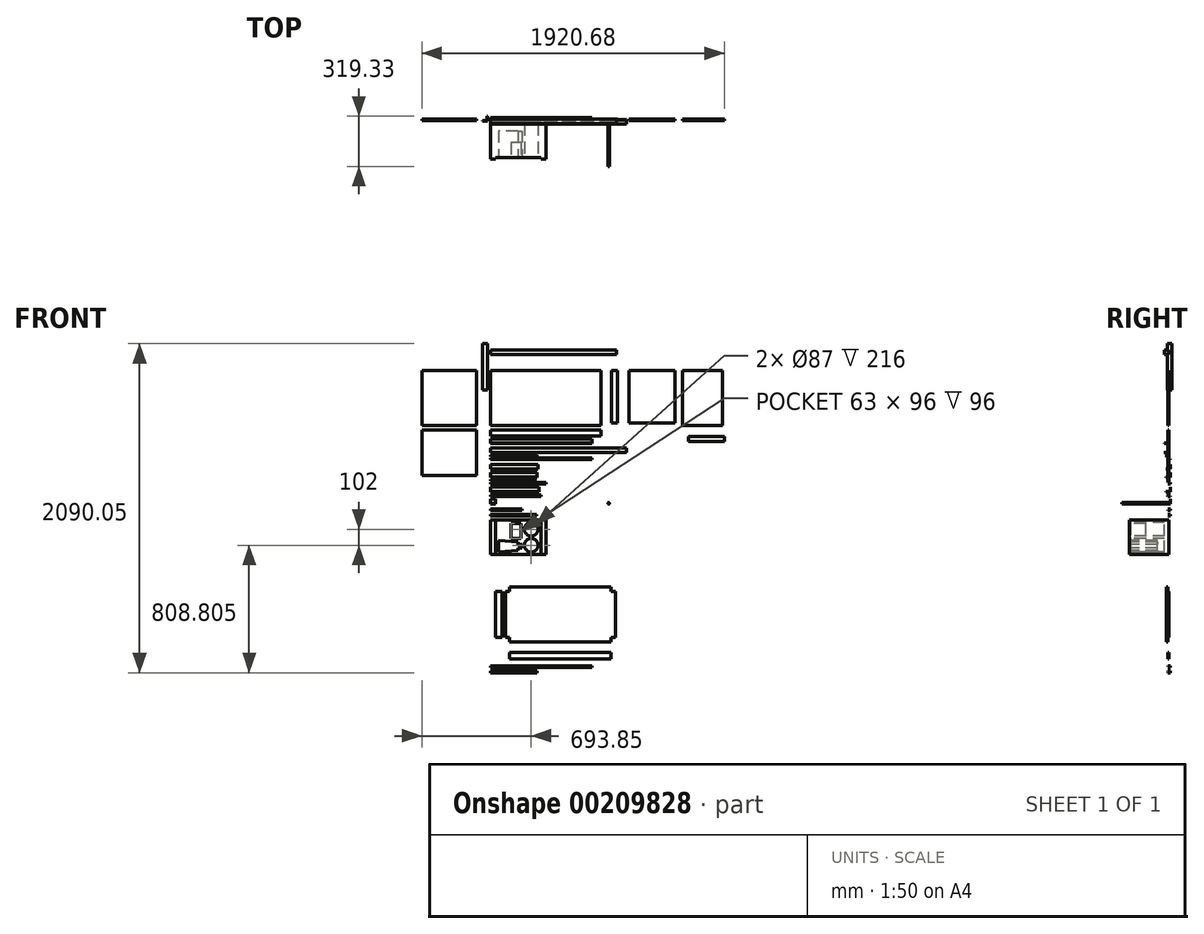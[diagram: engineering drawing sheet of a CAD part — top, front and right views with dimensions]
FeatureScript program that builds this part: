
annotation { "Feature Type Name" : "Feature", "Feature Type Description" : "" }
export const myFeature = defineFeature(function(context is Context, id is Id, definition is map)
    precondition{}
    {
        {
            assignVariable(context, id + "F0", {"name" : "width", "anyValue" : 350});
        }
        {
            assignVariable(context, id + "F1", {"name" : "height", "anyValue" : 800});
        }
        {
            assignVariable(context, id + "F2", {"name" : "length", "anyValue" : 700});
        }
        {
            assignVariable(context, id + "F3", {"name" : "panelW", "anyValue" : 8});
        }
        {
            assignVariable(context, id + "F4", {"name" : "postW", "anyValue" : 28});
        }
        {
            assignVariable(context, id + "F5", {"name" : "sideH", "anyValue" : 40});
        }
        {
            assignVariable(context, id + "F6", {"name" : "profileW", "anyValue" : getVariable(context, 'postW') + 2});
        }
        {
            assignVariable(context, id + "F7", {"name" : "topHeight", "anyValue" : 290});
        }
        {
            assignVariable(context, id + "F8", {"name" : "boxW", "anyValue" : 227});
        }
        {
            assignVariable(context, id + "F9", {"name" : "boxH", "anyValue" : 260});
        }
        {
            assignVariable(context, id + "F10", {"name" : "boxS", "anyValue" : 30});
        }
        {
            var Q0;
            Q0=qCreatedBy(makeId("Front.planeOp"),FACE);
            var sketch = newSketch(context, id + "F11", { "sketchPlane" : qUnion([Q0])});
            skLineSegment(sketch, "E0.bottom", {"start": v(0, 254.27) * mm, "end": v(800, 254.27) * mm});
            skLineSegment(sketch, "E0.top", {"start": v(0, 226.27) * mm, "end": v(800, 226.27) * mm});
            skLineSegment(sketch, "E0.left", {"start": v(0, 254.27) * mm, "end": v(0, 226.27) * mm});
            skLineSegment(sketch, "E0.right", {"start": v(800, 254.27) * mm, "end": v(800, 226.27) * mm});
            skSolve(sketch);
        }
        {
            var Q0;
            Q0=makeQuery(id+"F11.imprint","IMPRINT",FACE,{"disambiguationData":[TD([[makeQuery(id+"F11.imprint","IMPRINT",EDGE,{"derivedFrom":sQuery(id+"F11.wireOp",EDGE,"E0.bottom")}),-1.0]])]});
            extrude(context, id + "F12", {"entities" : qUnion([Q0]), "depth" : (getVariable(context, 'postW')) * mm});
        }
        {
            var Q0;
            Q0=qCreatedBy(makeId("Front.planeOp"),FACE);
            var sketch = newSketch(context, id + "F13", { "sketchPlane" : qUnion([Q0])});
            skLineSegment(sketch, "E1.bottom", {"start": v(0, 124.45) * mm, "end": v(700, 124.45) * mm});
            skLineSegment(sketch, "E1.top", {"start": v(0, -225.55) * mm, "end": v(700, -225.55) * mm});
            skLineSegment(sketch, "E1.left", {"start": v(0, 124.45) * mm, "end": v(0, -225.55) * mm});
            skLineSegment(sketch, "E1.right", {"start": v(700, 124.45) * mm, "end": v(700, -225.55) * mm});
            skSolve(sketch);
        }
        {
            var Q0;
            Q0 = qSketchRegion(id + "F13", true);
            extrude(context, id + "F14", {"entities" : qUnion([Q0]), "depth" : (getVariable(context, 'panelW')) * mm});
        }
        {
            var Q0;
            Q0=qCreatedBy(makeId("Front.planeOp"),FACE);
            var sketch = newSketch(context, id + "F15", { "sketchPlane" : qUnion([Q0])});
            skLineSegment(sketch, "E2.bottom", {"start": v(0, -254.2) * mm, "end": v(700, -254.2) * mm});
            skLineSegment(sketch, "E2.top", {"start": v(0, -294.2) * mm, "end": v(700, -294.2) * mm});
            skLineSegment(sketch, "E2.left", {"start": v(0, -254.2) * mm, "end": v(0, -294.2) * mm});
            skLineSegment(sketch, "E2.right", {"start": v(700, -254.2) * mm, "end": v(700, -294.2) * mm});
            skSolve(sketch);
        }
        {
            var Q0;
            Q0 = qSketchRegion(id + "F15", true);
            extrude(context, id + "F16", {"entities" : qUnion([Q0]), "depth" : (getVariable(context, 'panelW')) * mm});
        }
        {
            var Q0;
            Q0=qCreatedBy(makeId("Front.planeOp"),FACE);
            var sketch = newSketch(context, id + "F17", { "sketchPlane" : qUnion([Q0])});
            skLineSegment(sketch, "E3.bottom", {"start": v(766.47, 124.45) * mm, "end": v(806.47, 124.45) * mm});
            skLineSegment(sketch, "E3.top", {"start": v(766.47, -209.55) * mm, "end": v(806.47, -209.55) * mm});
            skLineSegment(sketch, "E3.left", {"start": v(766.47, 124.45) * mm, "end": v(766.47, -209.55) * mm});
            skLineSegment(sketch, "E3.right", {"start": v(806.47, 124.45) * mm, "end": v(806.47, -209.55) * mm});
            skSolve(sketch);
        }
        {
            var Q0;
            Q0 = qSketchRegion(id + "F17", true);
            extrude(context, id + "F18", {"entities" : qUnion([Q0]), "depth" : (getVariable(context, 'panelW')) * mm});
        }
        {
            var Q0;
            Q0=qCreatedBy(makeId("Right.planeOp"),FACE);
            var sketch = newSketch(context, id + "F19", { "sketchPlane" : qUnion([Q0])});
            skLineSegment(sketch, "E4", {"start": v(0, -310.42) * mm, "end": v(0, -340.42) * mm});
            skLineSegment(sketch, "E5", {"start": v(0, -340.42) * mm, "end": v(-30, -340.42) * mm});
            skLineSegment(sketch, "E6", {"start": v(-30, -340.42) * mm, "end": v(-30, -338.42) * mm});
            skLineSegment(sketch, "E7", {"start": v(-30, -338.42) * mm, "end": v(-2, -338.42) * mm});
            skLineSegment(sketch, "E8", {"start": v(-2, -338.42) * mm, "end": v(-2, -310.42) * mm});
            skLineSegment(sketch, "E9", {"start": v(-2, -310.42) * mm, "end": v(0, -310.42) * mm});
            skSolve(sketch);
        }
        {
            var Q0;
            Q0 = qSketchRegion(id + "F19", true);
            extrude(context, id + "F20", {"entities" : qUnion([Q0]), "depth" : (getVariable(context, 'length') - 2 * getVariable(context, 'postW')) * mm});
        }
        {
            var Q0;
            Q0=qCreatedBy(makeId("Top.planeOp"),FACE);
            var sketch = newSketch(context, id + "F21", { "sketchPlane" : qUnion([Q0])});
            skLineSegment(sketch, "E10", {"start": v(-21.86, 19.33) * mm, "end": v(-21.86, -10.67) * mm});
            skLineSegment(sketch, "E11", {"start": v(-21.86, -10.67) * mm, "end": v(-51.86, -10.67) * mm});
            skLineSegment(sketch, "E12", {"start": v(-51.86, -10.67) * mm, "end": v(-51.86, -8.67) * mm});
            skLineSegment(sketch, "E13", {"start": v(-51.86, -8.67) * mm, "end": v(-23.86, -8.67) * mm});
            skLineSegment(sketch, "E14", {"start": v(-23.86, -8.67) * mm, "end": v(-23.86, 19.33) * mm});
            skLineSegment(sketch, "E15", {"start": v(-23.86, 19.33) * mm, "end": v(-21.86, 19.33) * mm});
            skSolve(sketch);
        }
        {
            var Q0;
            Q0 = qSketchRegion(id + "F21", true);
            extrude(context, id + "F22", {"entities" : qUnion([Q0]), "depth" : (getVariable(context, 'width') - 2 * getVariable(context, 'postW')) * mm});
        }
        {
            var Q0;
            Q0=makeQuery(id+"F14.opExtrude","SWEPT_FACE",FACE,{"disambiguationData":[OSD([sQuery(id+"F13.wireOp",EDGE,"E1.left")])]});
            var Q1;
            Q1=makeQuery(id+"F14.opExtrude","SWEPT_FACE",FACE,{"disambiguationData":[OSD([sQuery(id+"F13.wireOp",EDGE,"E1.right")])]});
            cPlane(context, id + "F23", {"entities" : qUnion([Q0, Q1]), "cplaneType" : CPlaneType.MID_PLANE, "offset" : 25 * mm, "width" : 150 * mm, "height" : 150 * mm});
        }
        {
            var Q0;
            Q0=qCreatedBy(makeId("Right.planeOp"),FACE);
            var sketch = newSketch(context, id + "F24", { "sketchPlane" : qUnion([Q0])});
            skLineSegment(sketch, "E16", {"start": v(-1.9, -368) * mm, "end": v(-1.9, -398) * mm});
            skLineSegment(sketch, "E17", {"start": v(-1.9, -398) * mm, "end": v(-31.9, -398) * mm});
            skLineSegment(sketch, "E18", {"start": v(-31.9, -398) * mm, "end": v(-31.9, -396) * mm});
            skLineSegment(sketch, "E19", {"start": v(-31.9, -396) * mm, "end": v(-3.9, -396) * mm});
            skLineSegment(sketch, "E20", {"start": v(-3.9, -396) * mm, "end": v(-3.9, -368) * mm});
            skLineSegment(sketch, "E21", {"start": v(-3.9, -368) * mm, "end": v(-1.9, -368) * mm});
            skSolve(sketch);
        }
        {
            var Q0;
            Q0 = qSketchRegion(id + "F24", true);
            extrude(context, id + "F25", {"entities" : qUnion([Q0]), "depth" : (getVariable(context, 'height') + getVariable(context, 'sideH') + 2 * getVariable(context, 'panelW') + 6) * mm});
        }
        {
            var Q0;
            Q0=qCreatedBy(makeId("Right.planeOp"),FACE);
            var sketch = newSketch(context, id + "F26", { "sketchPlane" : qUnion([Q0])});
            skLineSegment(sketch, "E22", {"start": v(0, -412.2) * mm, "end": v(-20.5, -412.2) * mm});
            skLineSegment(sketch, "E23", {"start": v(-20.5, -412.2) * mm, "end": v(-17.5, -415.2) * mm});
            skLineSegment(sketch, "E24", {"start": v(-17.5, -415.2) * mm, "end": v(-20.5, -418.2) * mm});
            skLineSegment(sketch, "E25", {"start": v(-20.5, -418.2) * mm, "end": v(-16.5, -422.2) * mm});
            skLineSegment(sketch, "E26", {"start": v(-16.5, -422.2) * mm, "end": v(0, -422.2) * mm});
            skLineSegment(sketch, "E27", {"start": v(0, -422.2) * mm, "end": v(0, -420.7) * mm});
            skLineSegment(sketch, "E28", {"start": v(0, -420.7) * mm, "end": v(-14.5, -420.7) * mm});
            skLineSegment(sketch, "E29", {"start": v(-14.5, -420.7) * mm, "end": v(-14.5, -413.7) * mm});
            skLineSegment(sketch, "E30", {"start": v(-14.5, -413.7) * mm, "end": v(0, -413.7) * mm});
            skLineSegment(sketch, "E31", {"start": v(0, -413.7) * mm, "end": v(0, -412.2) * mm});
            skSolve(sketch);
        }
        {
            var Q0;
            Q0 = qSketchRegion(id + "F26", true);
            extrude(context, id + "F27", {"entities" : qUnion([Q0]), "depth" : (getVariable(context, 'width') - 2 * getVariable(context, 'postW')) * mm});
        }
        {
            var Q0;
            Q0=qCreatedBy(makeId("Right.planeOp"),FACE);
            var sketch = newSketch(context, id + "F28", { "sketchPlane" : qUnion([Q0])});
            skLineSegment(sketch, "E32", {"start": v(10.4, -431.26) * mm, "end": v(-10.1, -431.26) * mm});
            skLineSegment(sketch, "E33", {"start": v(-10.1, -431.26) * mm, "end": v(-7.1, -434.26) * mm});
            skLineSegment(sketch, "E34", {"start": v(-7.1, -434.26) * mm, "end": v(-10.1, -437.26) * mm});
            skLineSegment(sketch, "E35", {"start": v(-10.1, -437.26) * mm, "end": v(-6.1, -441.26) * mm});
            skLineSegment(sketch, "E36", {"start": v(-6.1, -441.26) * mm, "end": v(10.4, -441.26) * mm});
            skLineSegment(sketch, "E37", {"start": v(10.4, -441.26) * mm, "end": v(10.4, -439.76) * mm});
            skLineSegment(sketch, "E38", {"start": v(10.4, -439.76) * mm, "end": v(-4.1, -439.76) * mm});
            skLineSegment(sketch, "E39", {"start": v(-4.1, -439.76) * mm, "end": v(-4.1, -432.76) * mm});
            skLineSegment(sketch, "E40", {"start": v(-4.1, -432.76) * mm, "end": v(10.4, -432.76) * mm});
            skLineSegment(sketch, "E41", {"start": v(10.4, -432.76) * mm, "end": v(10.4, -431.26) * mm});
            skSolve(sketch);
        }
        {
            var Q0;
            Q0 = qSketchRegion(id + "F28", true);
            extrude(context, id + "F29", {"entities" : qUnion([Q0]), "depth" : (getVariable(context, 'length') - 2 * getVariable(context, 'postW')) * mm});
        }
        {
            var Q0;
            Q0=qCreatedBy(makeId("Front.planeOp"),FACE);
            var sketch = newSketch(context, id + "F30", { "sketchPlane" : qUnion([Q0])});
            skLineSegment(sketch, "E42.bottom", {"start": v(879.27, 124.45) * mm, "end": v(1169.27, 124.45) * mm});
            skLineSegment(sketch, "E42.top", {"start": v(879.27, -209.55) * mm, "end": v(1169.27, -209.55) * mm});
            skLineSegment(sketch, "E42.left", {"start": v(879.27, 124.45) * mm, "end": v(879.27, -209.55) * mm});
            skLineSegment(sketch, "E42.right", {"start": v(1169.27, 124.45) * mm, "end": v(1169.27, -209.55) * mm});
            skSolve(sketch);
        }
        {
            var Q0;
            Q0 = qSketchRegion(id + "F30", true);
            extrude(context, id + "F31", {"entities" : qUnion([Q0]), "depth" : (getVariable(context, 'panelW')) * mm});
        }
        {
            var Q0;
            Q0=qCreatedBy(makeId("Front.planeOp"),FACE);
            var sketch = newSketch(context, id + "F32", { "sketchPlane" : qUnion([Q0])});
            skLineSegment(sketch, "E43.bottom", {"start": v(-88.85, 124.45) * mm, "end": v(-437.35, 124.45) * mm});
            skLineSegment(sketch, "E43.top", {"start": v(-88.85, -225.55) * mm, "end": v(-437.35, -225.55) * mm});
            skLineSegment(sketch, "E43.left", {"start": v(-88.85, 124.45) * mm, "end": v(-88.85, -225.55) * mm});
            skLineSegment(sketch, "E43.right", {"start": v(-437.35, 124.45) * mm, "end": v(-437.35, -225.55) * mm});
            skSolve(sketch);
        }
        {
            var Q0;
            Q0 = qSketchRegion(id + "F32", true);
            extrude(context, id + "F33", {"entities" : qUnion([Q0]), "depth" : (getVariable(context, 'panelW')) * mm});
        }
        {
            var Q0;
            Q0=qCreatedBy(makeId("Front.planeOp"),FACE);
            var sketch = newSketch(context, id + "F34", { "sketchPlane" : qUnion([Q0])});
            skLineSegment(sketch, "E44.bottom", {"start": v(-437.35, -254.2) * mm, "end": v(-88.85, -254.2) * mm});
            skLineSegment(sketch, "E44.top", {"start": v(-437.35, -544.2) * mm, "end": v(-88.85, -544.2) * mm});
            skLineSegment(sketch, "E44.left", {"start": v(-437.35, -254.2) * mm, "end": v(-437.35, -544.2) * mm});
            skLineSegment(sketch, "E44.right", {"start": v(-88.85, -254.2) * mm, "end": v(-88.85, -544.2) * mm});
            skSolve(sketch);
        }
        {
            var Q0;
            Q0 = qSketchRegion(id + "F34", true);
            extrude(context, id + "F35", {"entities" : qUnion([Q0]), "depth" : (getVariable(context, 'panelW')) * mm});
        }
        {
            var Q0;
            Q0=qCreatedBy(makeId("Right.planeOp"),FACE);
            var sketch = newSketch(context, id + "F36", { "sketchPlane" : qUnion([Q0])});
            skLineSegment(sketch, "E45", {"start": v(10.67, -472.68) * mm, "end": v(10.67, -502.68) * mm});
            skLineSegment(sketch, "E46", {"start": v(10.67, -502.68) * mm, "end": v(-19.33, -502.68) * mm});
            skLineSegment(sketch, "E47", {"start": v(-19.33, -502.68) * mm, "end": v(-19.33, -500.68) * mm});
            skLineSegment(sketch, "E48", {"start": v(-19.33, -500.68) * mm, "end": v(8.67, -500.68) * mm});
            skLineSegment(sketch, "E49", {"start": v(8.67, -500.68) * mm, "end": v(8.67, -472.68) * mm});
            skLineSegment(sketch, "E50", {"start": v(8.67, -472.68) * mm, "end": v(10.67, -472.68) * mm});
            skSolve(sketch);
        }
        {
            var Q0;
            Q0 = qSketchRegion(id + "F36", true);
            extrude(context, id + "F37", {"entities" : qUnion([Q0]), "depth" : (getVariable(context, 'topHeight') + getVariable(context, 'panelW') + 2) * mm});
        }
        {
            var Q0;
            Q0=qCreatedBy(makeId("Right.planeOp"),FACE);
            var sketch = newSketch(context, id + "F38", { "sketchPlane" : qUnion([Q0])});
            skLineSegment(sketch, "E51", {"start": v(10.67, -524.8) * mm, "end": v(10.67, -554.8) * mm});
            skLineSegment(sketch, "E52", {"start": v(10.67, -554.8) * mm, "end": v(-19.33, -554.8) * mm});
            skLineSegment(sketch, "E53", {"start": v(-19.33, -554.8) * mm, "end": v(-19.33, -552.8) * mm});
            skLineSegment(sketch, "E54", {"start": v(-19.33, -552.8) * mm, "end": v(8.67, -552.8) * mm});
            skLineSegment(sketch, "E55", {"start": v(8.67, -552.8) * mm, "end": v(8.67, -524.8) * mm});
            skLineSegment(sketch, "E56", {"start": v(8.67, -524.8) * mm, "end": v(10.67, -524.8) * mm});
            skSolve(sketch);
        }
        {
            var Q0;
            Q0 = qSketchRegion(id + "F38", true);
            extrude(context, id + "F39", {"entities" : qUnion([Q0]), "depth" : (getVariable(context, 'width') - 2 * getVariable(context, 'profileW') + 2 * 2) * mm});
        }
        {
            var Q0;
            Q0=qCreatedBy(makeId("Right.planeOp"),FACE);
            var sketch = newSketch(context, id + "F40", { "sketchPlane" : qUnion([Q0])});
            skLineSegment(sketch, "E57", {"start": v(-16.5, -568.56) * mm, "end": v(0, -568.56) * mm});
            skLineSegment(sketch, "E58", {"start": v(0, -568.56) * mm, "end": v(0, -578.56) * mm});
            skLineSegment(sketch, "E59", {"start": v(0, -578.56) * mm, "end": v(-16.5, -578.56) * mm});
            skLineSegment(sketch, "E60", {"start": v(-16.5, -578.56) * mm, "end": v(-16.5, -577.06) * mm});
            skLineSegment(sketch, "E61", {"start": v(-16.5, -577.06) * mm, "end": v(-1.5, -577.06) * mm});
            skLineSegment(sketch, "E62", {"start": v(-1.5, -577.06) * mm, "end": v(-1.5, -570.06) * mm});
            skLineSegment(sketch, "E63", {"start": v(-1.5, -570.06) * mm, "end": v(-16.5, -570.06) * mm});
            skLineSegment(sketch, "E64", {"start": v(-16.5, -570.06) * mm, "end": v(-16.5, -568.56) * mm});
            skSolve(sketch);
        }
        {
            var Q0;
            Q0 = qSketchRegion(id + "F40", true);
            extrude(context, id + "F41", {"entities" : qUnion([Q0]), "depth" : (getVariable(context, 'topHeight') - 7.5) * mm});
        }
        {
            var Q0;
            Q0=qCreatedBy(makeId("Right.planeOp"),FACE);
            var sketch = newSketch(context, id + "F42", { "sketchPlane" : qUnion([Q0])});
            skLineSegment(sketch, "E65", {"start": v(-7.75, -587.4) * mm, "end": v(8.75, -587.4) * mm});
            skLineSegment(sketch, "E66", {"start": v(8.75, -587.4) * mm, "end": v(8.75, -597.4) * mm});
            skLineSegment(sketch, "E67", {"start": v(8.75, -597.4) * mm, "end": v(-7.75, -597.4) * mm});
            skLineSegment(sketch, "E68", {"start": v(-7.75, -597.4) * mm, "end": v(-7.75, -595.9) * mm});
            skLineSegment(sketch, "E69", {"start": v(-7.75, -595.9) * mm, "end": v(7.25, -595.9) * mm});
            skLineSegment(sketch, "E70", {"start": v(7.25, -595.9) * mm, "end": v(7.25, -588.9) * mm});
            skLineSegment(sketch, "E71", {"start": v(7.25, -588.9) * mm, "end": v(-7.75, -588.9) * mm});
            skLineSegment(sketch, "E72", {"start": v(-7.75, -588.9) * mm, "end": v(-7.75, -587.4) * mm});
            skSolve(sketch);
        }
        {
            var Q0;
            Q0 = qSketchRegion(id + "F42", true);
            extrude(context, id + "F43", {"entities" : qUnion([Q0]), "depth" : (getVariable(context, 'width')) * mm});
        }
        {
            var Q0;
            Q0=qCreatedBy(makeId("Right.planeOp"),FACE);
            var sketch = newSketch(context, id + "F44", { "sketchPlane" : qUnion([Q0])});
            skLineSegment(sketch, "E73", {"start": v(10.67, -616.68) * mm, "end": v(10.67, -646.68) * mm});
            skLineSegment(sketch, "E74", {"start": v(10.67, -646.68) * mm, "end": v(-19.33, -646.68) * mm});
            skLineSegment(sketch, "E75", {"start": v(-19.33, -646.68) * mm, "end": v(-19.33, -644.68) * mm});
            skLineSegment(sketch, "E76", {"start": v(-19.33, -644.68) * mm, "end": v(8.67, -644.68) * mm});
            skLineSegment(sketch, "E77", {"start": v(8.67, -644.68) * mm, "end": v(8.67, -616.68) * mm});
            skLineSegment(sketch, "E78", {"start": v(8.67, -616.68) * mm, "end": v(10.67, -616.68) * mm});
            skSolve(sketch);
        }
        {
            var Q0;
            Q0 = qSketchRegion(id + "F44", true);
            extrude(context, id + "F45", {"entities" : qUnion([Q0]), "depth" : (getVariable(context, 'length') / 2 - 1.5 - getVariable(context, 'profileW') + 2 - 15) * mm});
        }
        {
            var Q0;
            Q0=qCreatedBy(makeId("Right.planeOp"),FACE);
            var sketch = newSketch(context, id + "F46", { "sketchPlane" : qUnion([Q0])});
            skLineSegment(sketch, "E79", {"start": v(10.4, -665.74) * mm, "end": v(-10.1, -665.74) * mm});
            skLineSegment(sketch, "E80", {"start": v(-10.1, -665.74) * mm, "end": v(-7.1, -668.74) * mm});
            skLineSegment(sketch, "E81", {"start": v(-7.1, -668.74) * mm, "end": v(-10.1, -671.74) * mm});
            skLineSegment(sketch, "E82", {"start": v(-10.1, -671.74) * mm, "end": v(-6.1, -675.74) * mm});
            skLineSegment(sketch, "E83", {"start": v(-6.1, -675.74) * mm, "end": v(10.4, -675.74) * mm});
            skLineSegment(sketch, "E84", {"start": v(10.4, -675.74) * mm, "end": v(10.4, -674.24) * mm});
            skLineSegment(sketch, "E85", {"start": v(10.4, -674.24) * mm, "end": v(-4.1, -674.24) * mm});
            skLineSegment(sketch, "E86", {"start": v(-4.1, -674.24) * mm, "end": v(-4.1, -667.24) * mm});
            skLineSegment(sketch, "E87", {"start": v(-4.1, -667.24) * mm, "end": v(10.4, -667.24) * mm});
            skLineSegment(sketch, "E88", {"start": v(10.4, -667.24) * mm, "end": v(10.4, -665.74) * mm});
            skSolve(sketch);
        }
        {
            var Q0;
            Q0 = qSketchRegion(id + "F46", true);
            extrude(context, id + "F47", {"entities" : qUnion([Q0]), "depth" : (getVariable(context, 'length') / 2 - 1.5 - getVariable(context, 'profileW') + 2) * mm});
        }
        {
            var Q0;
            Q0=qCreatedBy(makeId("Front.planeOp"),FACE);
            var sketch = newSketch(context, id + "F48", { "sketchPlane" : qUnion([Q0])});
            skLineSegment(sketch, "E89.bottom", {"start": v(1218.72, 124.45) * mm, "end": v(1470.72, 124.45) * mm});
            skLineSegment(sketch, "E89.top", {"start": v(1218.72, -225.55) * mm, "end": v(1470.72, -225.55) * mm});
            skLineSegment(sketch, "E89.left", {"start": v(1218.72, 124.45) * mm, "end": v(1218.72, -225.55) * mm});
            skLineSegment(sketch, "E89.right", {"start": v(1470.72, 124.45) * mm, "end": v(1470.72, -225.55) * mm});
            skSolve(sketch);
        }
        {
            var Q0;
            Q0=makeQuery(id+"F48.imprint","IMPRINT",FACE,{"disambiguationData":[TD([[makeQuery(id+"F48.imprint","IMPRINT",EDGE,{"derivedFrom":sQuery(id+"F48.wireOp",EDGE,"E89.bottom")}),-1.0]])]});
            var Q1;
            Q1 = qSketchRegion(id + "F48", true);
            extrude(context, id + "F49", {"entities" : qUnion([Q0, Q1]), "depth" : (getVariable(context, 'panelW')) * mm});
        }
        {
            var Q0;
            Q0=qCreatedBy(makeId("Front.planeOp"),FACE);
            var sketch = newSketch(context, id + "F50", { "sketchPlane" : qUnion([Q0])});
            skLineSegment(sketch, "E90.bottom", {"start": v(1256.33, -296.54) * mm, "end": v(1483.33, -296.54) * mm});
            skLineSegment(sketch, "E90.top", {"start": v(1256.33, -326.54) * mm, "end": v(1483.33, -326.54) * mm});
            skLineSegment(sketch, "E90.left", {"start": v(1256.33, -296.54) * mm, "end": v(1256.33, -326.54) * mm});
            skLineSegment(sketch, "E90.right", {"start": v(1483.33, -296.54) * mm, "end": v(1483.33, -326.54) * mm});
            skSolve(sketch);
        }
        {
            var Q0;
            Q0 = qSketchRegion(id + "F50", true);
            extrude(context, id + "F51", {"entities" : qUnion([Q0]), "depth" : (getVariable(context, 'panelW')) * mm});
        }
        {
            var Q0;
            Q0=qCreatedBy(makeId("Right.planeOp"),FACE);
            var sketch = newSketch(context, id + "F52", { "sketchPlane" : qUnion([Q0])});
            skLineSegment(sketch, "E91", {"start": v(10.67, -693.54) * mm, "end": v(10.67, -723.54) * mm});
            skLineSegment(sketch, "E92", {"start": v(10.67, -723.54) * mm, "end": v(-19.33, -723.54) * mm});
            skLineSegment(sketch, "E93", {"start": v(-19.33, -723.54) * mm, "end": v(-19.33, -721.54) * mm});
            skLineSegment(sketch, "E94", {"start": v(-19.33, -721.54) * mm, "end": v(8.67, -721.54) * mm});
            skLineSegment(sketch, "E95", {"start": v(8.67, -721.54) * mm, "end": v(8.67, -693.54) * mm});
            skLineSegment(sketch, "E96", {"start": v(8.67, -693.54) * mm, "end": v(10.67, -693.54) * mm});
            skSolve(sketch);
        }
        {
            var Q0;
            Q0 = qSketchRegion(id + "F52", true);
            extrude(context, id + "F53", {"entities" : qUnion([Q0]), "depth" : (getVariable(context, 'boxS')) * mm});
        }
        {
            var Q0;
            Q0=qCreatedBy(makeId("Right.planeOp"),FACE);
            var sketch = newSketch(context, id + "F54", { "sketchPlane" : qUnion([Q0])});
            skLineSegment(sketch, "E97", {"start": v(-7.75, -755.1) * mm, "end": v(8.75, -755.1) * mm});
            skLineSegment(sketch, "E98", {"start": v(8.75, -755.1) * mm, "end": v(8.75, -765.1) * mm});
            skLineSegment(sketch, "E99", {"start": v(8.75, -765.1) * mm, "end": v(-7.75, -765.1) * mm});
            skLineSegment(sketch, "E100", {"start": v(-7.75, -765.1) * mm, "end": v(-7.75, -763.6) * mm});
            skLineSegment(sketch, "E101", {"start": v(-7.75, -763.6) * mm, "end": v(7.25, -763.6) * mm});
            skLineSegment(sketch, "E102", {"start": v(7.25, -763.6) * mm, "end": v(7.25, -756.6) * mm});
            skLineSegment(sketch, "E103", {"start": v(7.25, -756.6) * mm, "end": v(-7.75, -756.6) * mm});
            skLineSegment(sketch, "E104", {"start": v(-7.75, -756.6) * mm, "end": v(-7.75, -755.1) * mm});
            skSolve(sketch);
        }
        {
            var Q0;
            Q0 = qSketchRegion(id + "F54", true);
            extrude(context, id + "F55", {"entities" : qUnion([Q0]), "depth" : (getVariable(context, 'boxW') - getVariable(context, 'profileW') + 2) * mm});
        }
        {
            var Q0;
            Q0=qCreatedBy(makeId("Right.planeOp"),FACE);
            var sketch = newSketch(context, id + "F56", { "sketchPlane" : qUnion([Q0])});
            skLineSegment(sketch, "E105", {"start": v(-7.75, -790.94) * mm, "end": v(8.75, -790.94) * mm});
            skLineSegment(sketch, "E106", {"start": v(8.75, -790.94) * mm, "end": v(8.75, -800.94) * mm});
            skLineSegment(sketch, "E107", {"start": v(8.75, -800.94) * mm, "end": v(-7.75, -800.94) * mm});
            skLineSegment(sketch, "E108", {"start": v(-7.75, -800.94) * mm, "end": v(-7.75, -799.44) * mm});
            skLineSegment(sketch, "E109", {"start": v(-7.75, -799.44) * mm, "end": v(7.25, -799.44) * mm});
            skLineSegment(sketch, "E110", {"start": v(7.25, -799.44) * mm, "end": v(7.25, -792.44) * mm});
            skLineSegment(sketch, "E111", {"start": v(7.25, -792.44) * mm, "end": v(-7.75, -792.44) * mm});
            skLineSegment(sketch, "E112", {"start": v(-7.75, -792.44) * mm, "end": v(-7.75, -790.94) * mm});
            skSolve(sketch);
        }
        {
            var Q0;
            Q0 = qSketchRegion(id + "F56", true);
            extrude(context, id + "F57", {"entities" : qUnion([Q0]), "depth" : (getVariable(context, 'width') - 2 * getVariable(context, 'boxS')) * mm});
        }
        {
            var Q0;
            Q0=qCreatedBy(makeId("Front.planeOp"),FACE);
            var sketch = newSketch(context, id + "F58", { "sketchPlane" : qUnion([Q0])});
            skLineSegment(sketch, "E113.bottom", {"start": v(0, -826.74) * mm, "end": v(350, -826.74) * mm});
            skLineSegment(sketch, "E113.top", {"start": v(0, -1045.74) * mm, "end": v(350, -1045.74) * mm});
            skLineSegment(sketch, "E113.left", {"start": v(0, -826.74) * mm, "end": v(0, -1045.74) * mm});
            skLineSegment(sketch, "E113.right", {"start": v(350, -826.74) * mm, "end": v(350, -1045.74) * mm});
            skSolve(sketch);
        }
        {
            var Q0;
            Q0=makeQuery(id+"F58.imprint","IMPRINT",FACE,{"disambiguationData":[TD([[makeQuery(id+"F58.imprint","IMPRINT",EDGE,{"derivedFrom":sQuery(id+"F58.wireOp",EDGE,"E113.bottom")}),-1.0]])]});
            extrude(context, id + "F59", {"entities" : qUnion([Q0]), "depth" : (getVariable(context, 'boxH') - getVariable(context, 'panelW')) * mm});
        }
        {
            var Q0;
            Q0=makeQuery(id+"F59.opExtrude","CAP_FACE",FACE,{"disambiguationData":[OSD([sQuery(id+"F58.wireOp",EDGE,"E113.bottom"),sQuery(id+"F58.wireOp",EDGE,"E113.top"),sQuery(id+"F58.wireOp",EDGE,"E113.left"),sQuery(id+"F58.wireOp",EDGE,"E113.right")])],"isStart":false});
            var sketch = newSketch(context, id + "F60", { "sketchPlane" : qUnion([Q0])});
            skLineSegment(sketch, "E114.bottom", {"start": v(30, -826.74) * mm, "end": v(320, -826.74) * mm});
            skLineSegment(sketch, "E114.top", {"start": v(30, -1045.74) * mm, "end": v(320, -1045.74) * mm});
            skLineSegment(sketch, "E114.left", {"start": v(30, -826.74) * mm, "end": v(30, -1045.74) * mm});
            skLineSegment(sketch, "E114.right", {"start": v(320, -826.74) * mm, "end": v(320, -1045.74) * mm});
            skSolve(sketch);
        }
        {
            var Q0;
            Q0 = qSketchRegion(id + "F60", true);
            extrude(context, id + "F61", {"entities" : qUnion([Q0]), "operationType" : NewBodyOperationType.REMOVE, "oppositeDirection" : true, "depth" : (getVariable(context, 'panelW')) * mm});
        }
        {
            var Q0;
            Q0=makeQuery(id+"F61.boolean.opBoolean","COPY",FACE,{"derivedFrom":makeQuery(id+"F61.opExtrude","CAP_FACE",FACE,{"disambiguationData":[OSD([sQuery(id+"F60.wireOp",EDGE,"E114.bottom"),sQuery(id+"F60.wireOp",EDGE,"E114.top"),sQuery(id+"F60.wireOp",EDGE,"E114.left"),sQuery(id+"F60.wireOp",EDGE,"E114.right")])],"isStart":false})});
            var sketch = newSketch(context, id + "F62", { "sketchPlane" : qUnion([Q0])});
            skCircle(sketch, "E115", {"center": v(256.5, -885.24) * mm, "radius": 43.5 * mm});
            skCircle(sketch, "E116", {"center": v(256.5, -987.24) * mm, "radius": 43.5 * mm});
            skSolve(sketch);
        }
        {
            var Q0;
            Q0 = qSketchRegion(id + "F62", true);
            extrude(context, id + "F63", {"entities" : qUnion([Q0]), "operationType" : NewBodyOperationType.REMOVE, "oppositeDirection" : true, "depth" : 216 * mm});
        }
        {
            var Q0;
            Q0=makeQuery(id+"F61.boolean.opBoolean","COPY",FACE,{"derivedFrom":makeQuery(id+"F61.opExtrude","CAP_FACE",FACE,{"disambiguationData":[OSD([sQuery(id+"F60.wireOp",EDGE,"E114.bottom"),sQuery(id+"F60.wireOp",EDGE,"E114.top"),sQuery(id+"F60.wireOp",EDGE,"E114.left"),sQuery(id+"F60.wireOp",EDGE,"E114.right")])],"isStart":false})});
            var sketch = newSketch(context, id + "F64", { "sketchPlane" : qUnion([Q0])});
            skLineSegment(sketch, "E117.bottom", {"start": v(193, -846.74) * mm, "end": v(130, -846.74) * mm});
            skLineSegment(sketch, "E117.top", {"start": v(193, -942.74) * mm, "end": v(130, -942.74) * mm});
            skLineSegment(sketch, "E117.left", {"start": v(193, -846.74) * mm, "end": v(193, -942.74) * mm});
            skLineSegment(sketch, "E117.right", {"start": v(130, -846.74) * mm, "end": v(130, -942.74) * mm});
            skSolve(sketch);
        }
        {
            var Q0;
            Q0 = qSketchRegion(id + "F64", true);
            extrude(context, id + "F65", {"entities" : qUnion([Q0]), "operationType" : NewBodyOperationType.REMOVE, "oppositeDirection" : true, "depth" : (48 * 2) * mm});
        }
        {
            var Q0;
            Q0=makeQuery(id+"F61.boolean.opBoolean","COPY",FACE,{"derivedFrom":makeQuery(id+"F61.opExtrude","CAP_FACE",FACE,{"disambiguationData":[OSD([sQuery(id+"F60.wireOp",EDGE,"E114.bottom"),sQuery(id+"F60.wireOp",EDGE,"E114.top"),sQuery(id+"F60.wireOp",EDGE,"E114.left"),sQuery(id+"F60.wireOp",EDGE,"E114.right")])],"isStart":false})});
            var sketch = newSketch(context, id + "F66", { "sketchPlane" : qUnion([Q0])});
            skLineSegment(sketch, "E118", {"start": v(173, -1019.74) * mm, "end": v(51, -1030.74) * mm});
            skLineSegment(sketch, "E119", {"start": v(173, -1019.74) * mm, "end": v(173, -1005.24) * mm});
            skLineSegment(sketch, "E120", {"start": v(173, -992.74) * mm, "end": v(51, -992.74) * mm, "construction": true});
            skLineSegment(sketch, "E121", {"start": v(51, -992.74) * mm, "end": v(51, -1030.74) * mm});
            skLineSegment(sketch, "E122", {"start": v(173, -1005.24) * mm, "end": v(198, -1005.24) * mm});
            skLineSegment(sketch, "E123", {"start": v(198, -1005.24) * mm, "end": v(198, -992.74) * mm});
            skLineSegment(sketch, "E124", {"start": v(198, -992.74) * mm, "end": v(173, -992.74) * mm, "construction": true});
            skLineSegment(sketch, "E125.MirrorCS", {"start": v(51, -992.74) * mm, "end": v(51, -954.74) * mm});
            skLineSegment(sketch, "E126.MirrorCS", {"start": v(173, -965.74) * mm, "end": v(51, -954.74) * mm});
            skLineSegment(sketch, "E127.MirrorCS", {"start": v(173, -965.74) * mm, "end": v(173, -980.24) * mm});
            skLineSegment(sketch, "E128.MirrorCS", {"start": v(173, -980.24) * mm, "end": v(198, -980.24) * mm});
            skLineSegment(sketch, "E129.MirrorCS", {"start": v(198, -980.24) * mm, "end": v(198, -992.74) * mm});
            skSolve(sketch);
        }
        {
            var Q0;
            Q0 = qSketchRegion(id + "F66", true);
            extrude(context, id + "F67", {"entities" : qUnion([Q0]), "operationType" : NewBodyOperationType.REMOVE, "oppositeDirection" : true, "depth" : 170 * mm});
        }
        {
            var Q0;
            Q0=qCreatedBy(makeId("Front.planeOp"),FACE);
            var sketch = newSketch(context, id + "F68", { "sketchPlane" : qUnion([Q0])});
            skCircle(sketch, "E130", {"center": v(749.37, -720.76) * mm, "radius": 5 * mm});
            skSolve(sketch);
        }
        {
            var Q0;
            Q0 = qSketchRegion(id + "F68", true);
            extrude(context, id + "F69", {"entities" : qUnion([Q0]), "depth" : 300 * mm});
        }
        {
            var Q0;
            Q0=makeQuery(id+"F14.opExtrude","CAP_FACE",FACE,{"disambiguationData":[OSD([sQuery(id+"F13.wireOp",EDGE,"E1.bottom"),sQuery(id+"F13.wireOp",EDGE,"E1.top"),sQuery(id+"F13.wireOp",EDGE,"E1.left"),sQuery(id+"F13.wireOp",EDGE,"E1.right")])],"isStart":false});
            var sketch = newSketch(context, id + "F70", { "sketchPlane" : qUnion([Q0])});
            skLineSegment(sketch, "E131.bottom", {"start": v(120.57, -1251) * mm, "end": v(764.57, -1251) * mm});
            skLineSegment(sketch, "E131.top", {"start": v(120.57, -1601) * mm, "end": v(764.57, -1601) * mm});
            skLineSegment(sketch, "E131.left", {"start": v(92.57, -1279) * mm, "end": v(92.57, -1573) * mm});
            skLineSegment(sketch, "E131.right", {"start": v(792.57, -1279) * mm, "end": v(792.57, -1573) * mm});
            skLineSegment(sketch, "E132", {"start": v(92.57, -1279) * mm, "end": v(120.57, -1279) * mm});
            skLineSegment(sketch, "E133", {"start": v(120.57, -1279) * mm, "end": v(120.57, -1251) * mm});
            skLineSegment(sketch, "E134", {"start": v(92.57, -1426) * mm, "end": v(792.57, -1426) * mm, "construction": true});
            skLineSegment(sketch, "E135", {"start": v(442.57, -1251) * mm, "end": v(442.57, -1601) * mm, "construction": true});
            skLineSegment(sketch, "E136.MirrorCS", {"start": v(92.57, -1573) * mm, "end": v(120.57, -1573) * mm});
            skLineSegment(sketch, "E137.MirrorCS", {"start": v(120.57, -1573) * mm, "end": v(120.57, -1601) * mm});
            skLineSegment(sketch, "E138.MirrorCS", {"start": v(792.57, -1279) * mm, "end": v(764.57, -1279) * mm});
            skLineSegment(sketch, "E139.MirrorCS", {"start": v(764.57, -1279) * mm, "end": v(764.57, -1251) * mm});
            skLineSegment(sketch, "E140.MirrorCS", {"start": v(792.57, -1573) * mm, "end": v(764.57, -1573) * mm});
            skLineSegment(sketch, "E141.MirrorCS", {"start": v(764.57, -1573) * mm, "end": v(764.57, -1601) * mm});
            skPoint(sketch, "E142.orphan", {"position": v(92.57, -1251) * mm});
            skPoint(sketch, "E143.orphan", {"position": v(92.57, -1601) * mm});
            skPoint(sketch, "E144.orphan", {"position": v(792.57, -1601) * mm});
            skPoint(sketch, "E145.orphan", {"position": v(792.57, -1251) * mm});
            skSolve(sketch);
        }
        {
            var Q0;
            Q0 = qSketchRegion(id + "F70", true);
            extrude(context, id + "F71", {"entities" : qUnion([Q0]), "depth" : (getVariable(context, 'panelW')) * mm});
        }
        {
            var Q0;
            Q0=qCreatedBy(makeId("Front.planeOp"),FACE);
            var sketch = newSketch(context, id + "F72", { "sketchPlane" : qUnion([Q0])});
            skLineSegment(sketch, "E146.bottom", {"start": v(120.57, -1668.04) * mm, "end": v(764.57, -1668.04) * mm});
            skLineSegment(sketch, "E146.top", {"start": v(120.57, -1708.04) * mm, "end": v(764.57, -1708.04) * mm});
            skLineSegment(sketch, "E146.left", {"start": v(120.57, -1668.04) * mm, "end": v(120.57, -1708.04) * mm});
            skLineSegment(sketch, "E146.right", {"start": v(764.57, -1668.04) * mm, "end": v(764.57, -1708.04) * mm});
            skSolve(sketch);
        }
        {
            var Q0;
            Q0=qCreatedBy(makeId("Front.planeOp"),FACE);
            var sketch = newSketch(context, id + "F73", { "sketchPlane" : qUnion([Q0])});
            skLineSegment(sketch, "E147.bottom", {"start": v(70.54, -1279) * mm, "end": v(30.54, -1279) * mm});
            skLineSegment(sketch, "E147.top", {"start": v(70.54, -1573) * mm, "end": v(30.54, -1573) * mm});
            skLineSegment(sketch, "E147.left", {"start": v(70.54, -1279) * mm, "end": v(70.54, -1573) * mm});
            skLineSegment(sketch, "E147.right", {"start": v(30.54, -1279) * mm, "end": v(30.54, -1573) * mm});
            skSolve(sketch);
        }
        {
            var Q0;
            Q0 = qSketchRegion(id + "F72", true);
            extrude(context, id + "F74", {"entities" : qUnion([Q0]), "depth" : (getVariable(context, 'panelW')) * mm});
        }
        {
            var Q0;
            Q0 = qSketchRegion(id + "F73", true);
            extrude(context, id + "F75", {"entities" : qUnion([Q0]), "depth" : (getVariable(context, 'panelW')) * mm});
        }
        {
            var Q0;
            Q0=qCreatedBy(makeId("Right.planeOp"),FACE);
            var sketch = newSketch(context, id + "F76", { "sketchPlane" : qUnion([Q0])});
            skLineSegment(sketch, "E148", {"start": v(-7.75, -1753.97) * mm, "end": v(8.25, -1753.97) * mm});
            skLineSegment(sketch, "E149", {"start": v(8.25, -1753.97) * mm, "end": v(8.25, -1763.97) * mm});
            skLineSegment(sketch, "E150", {"start": v(8.25, -1763.97) * mm, "end": v(-7.75, -1763.97) * mm});
            skLineSegment(sketch, "E151", {"start": v(-7.75, -1763.97) * mm, "end": v(-7.75, -1762.47) * mm});
            skLineSegment(sketch, "E152", {"start": v(-7.75, -1762.47) * mm, "end": v(7.25, -1762.47) * mm});
            skLineSegment(sketch, "E153", {"start": v(7.25, -1762.47) * mm, "end": v(7.25, -1755.47) * mm});
            skLineSegment(sketch, "E154", {"start": v(7.25, -1755.47) * mm, "end": v(-7.75, -1755.47) * mm});
            skLineSegment(sketch, "E155", {"start": v(-7.75, -1755.47) * mm, "end": v(-7.75, -1753.97) * mm});
            skSolve(sketch);
        }
        {
            var Q0;
            Q0=qCreatedBy(makeId("Right.planeOp"),FACE);
            var sketch = newSketch(context, id + "F77", { "sketchPlane" : qUnion([Q0])});
            skLineSegment(sketch, "E156", {"start": v(-7.75, -1786.05) * mm, "end": v(8.25, -1786.05) * mm});
            skLineSegment(sketch, "E157", {"start": v(8.25, -1786.05) * mm, "end": v(8.25, -1796.05) * mm});
            skLineSegment(sketch, "E158", {"start": v(8.25, -1796.05) * mm, "end": v(-7.75, -1796.05) * mm});
            skLineSegment(sketch, "E159", {"start": v(-7.75, -1796.05) * mm, "end": v(-7.75, -1794.55) * mm});
            skLineSegment(sketch, "E160", {"start": v(-7.75, -1794.55) * mm, "end": v(7.25, -1794.55) * mm});
            skLineSegment(sketch, "E161", {"start": v(7.25, -1794.55) * mm, "end": v(7.25, -1787.55) * mm});
            skLineSegment(sketch, "E162", {"start": v(7.25, -1787.55) * mm, "end": v(-7.75, -1787.55) * mm});
            skLineSegment(sketch, "E163", {"start": v(-7.75, -1787.55) * mm, "end": v(-7.75, -1786.05) * mm});
            skSolve(sketch);
        }
        {
            var Q0;
            Q0 = qSketchRegion(id + "F76", true);
            extrude(context, id + "F78", {"entities" : qUnion([Q0]), "depth" : (getVariable(context, 'length') - 2 * getVariable(context, 'postW')) * mm});
        }
        {
            var Q0;
            Q0 = qSketchRegion(id + "F77", true);
            extrude(context, id + "F79", {"entities" : qUnion([Q0]), "depth" : (getVariable(context, 'width') - 2 * getVariable(context, 'postW')) * mm});
        }
    });
